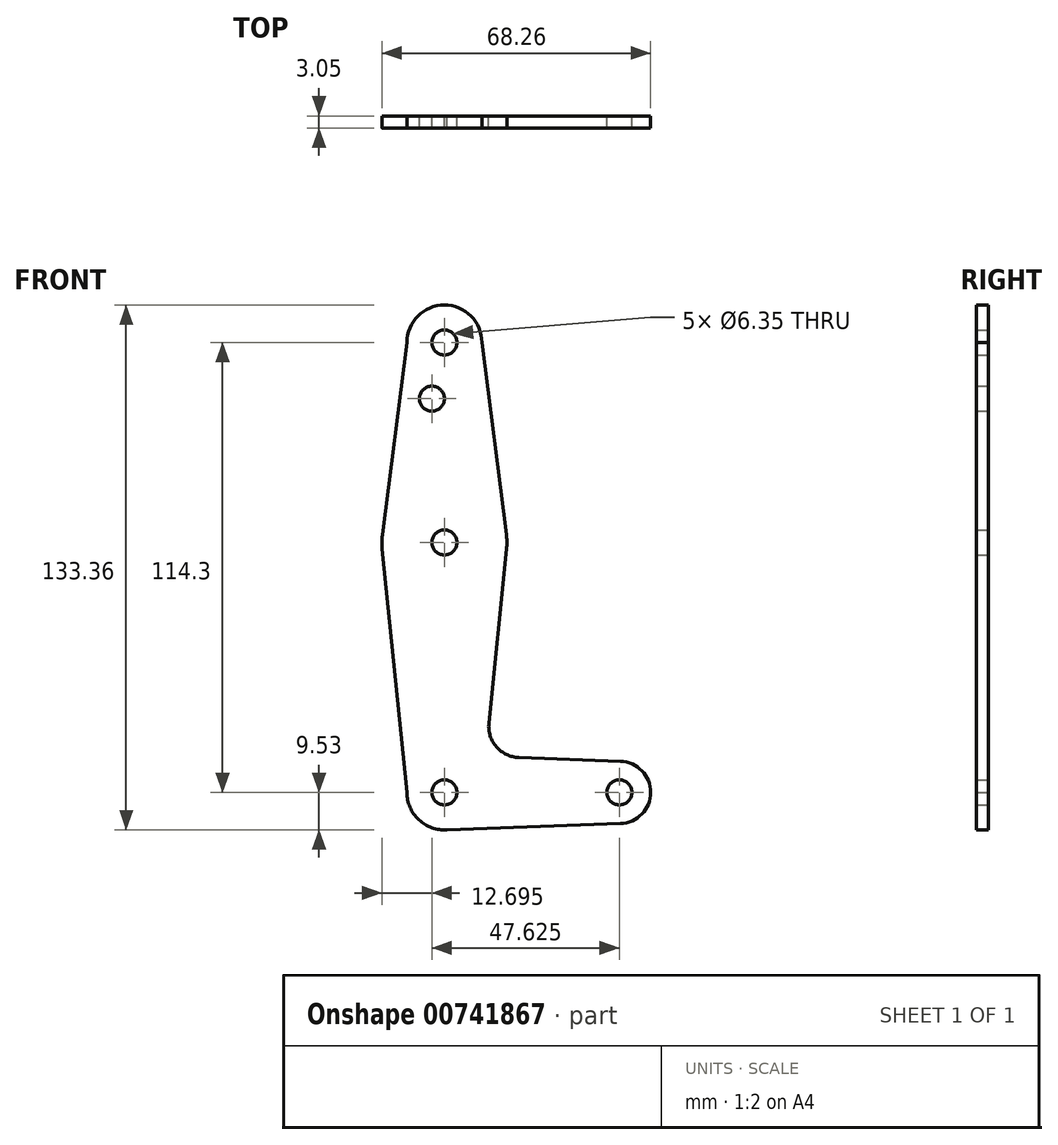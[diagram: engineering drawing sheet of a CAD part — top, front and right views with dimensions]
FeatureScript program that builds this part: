
annotation { "Feature Type Name" : "Feature", "Feature Type Description" : "" }
export const myFeature = defineFeature(function(context is Context, id is Id, definition is map)
    precondition{}
    {
        {
            var Q0;
            Q0=qCreatedBy(makeId("Front.planeOp"),FACE);
            var sketch = newSketch(context, id + "F0", { "sketchPlane" : qUnion([Q0])});
            skLineSegment(sketch, "E0", {"start": v(0, 0) * mm, "end": v(0, 114.3) * mm});
            skLineSegment(sketch, "E1", {"start": v(0, 0) * mm, "end": v(44.45, 0) * mm});
            skCircle(sketch, "E2", {"center": v(0, 0) * mm, "radius": 9.53 * mm});
            skCircle(sketch, "E3", {"center": v(44.45, 0) * mm, "radius": 7.94 * mm});
            skCircle(sketch, "E4", {"center": v(0, 114.3) * mm, "radius": 9.52 * mm});
            skCircle(sketch, "E5", {"center": v(0, 63.5) * mm, "radius": 15.88 * mm});
            skLineSegment(sketch, "E6", {"start": v(0, 0) * mm, "end": v(0, 63.5) * mm});
            skLineSegment(sketch, "E7", {"start": v(-9.52, 114.3) * mm, "end": v(-15.75, 65.5) * mm});
            skLineSegment(sketch, "E8", {"start": v(9.52, 114.3) * mm, "end": v(15.75, 65.5) * mm});
            skLineSegment(sketch, "E9", {"start": v(15.8, 61.9) * mm, "end": v(11.3, 17.6) * mm});
            skLineSegment(sketch, "E10", {"start": v(0, -9.53) * mm, "end": v(44.73, -7.93) * mm});
            skLineSegment(sketch, "E11", {"start": v(18.93, 8.85) * mm, "end": v(44.73, 7.93) * mm});
            skLineSegment(sketch, "E12", {"start": v(-15.8, 61.9) * mm, "end": v(-9.53, 0) * mm});
            skCircle(sketch, "E13", {"center": v(0, 114.3) * mm, "radius": 3.18 * mm});
            skCircle(sketch, "E14", {"center": v(0, 63.5) * mm, "radius": 3.18 * mm});
            skCircle(sketch, "E15", {"center": v(0, 0) * mm, "radius": 3.18 * mm});
            skCircle(sketch, "E16", {"center": v(44.45, 0) * mm, "radius": 3.18 * mm});
            skCircle(sketch, "E17", {"center": v(-3.17, 100.03) * mm, "radius": 3.18 * mm});
            skArc(sketch, "E18.filletArc", {"start": v(11.3, 17.6) * mm, "mid": v(13.22, 11.57) * mm, "end": v(18.93, 8.85) * mm});
            skSolve(sketch);
        }
        {
            var Q0;
            Q0 = qSketchRegion(id + "F0", true);
            var Q1;
            {var subQ0=sQuery(id+"F0.wireOp",EDGE,"E15");var subQ1=sQuery(id+"F0.wireOp",EDGE,"E1");var subQ2=makeQuery(id+"F0.imprint","INTERSECT",VERTEX,{"derivedFrom":[subQ1,subQ0]});Q1=makeQuery(id+"F0.imprint","IMPRINT",FACE,{"disambiguationData":[TD([[makeQuery(id+"F0.imprint","IMPRINT",EDGE,{"disambiguationData":[TD([[subQ2,-1.0]])],"derivedFrom":subQ1}),1.0]])]});}
            extrude(context, id + "F1", {"entities" : qUnion([Q0, Q1]), "depth" : 3.05 * mm, "offsetDistance" : 25.4 * mm});
        }
    });
